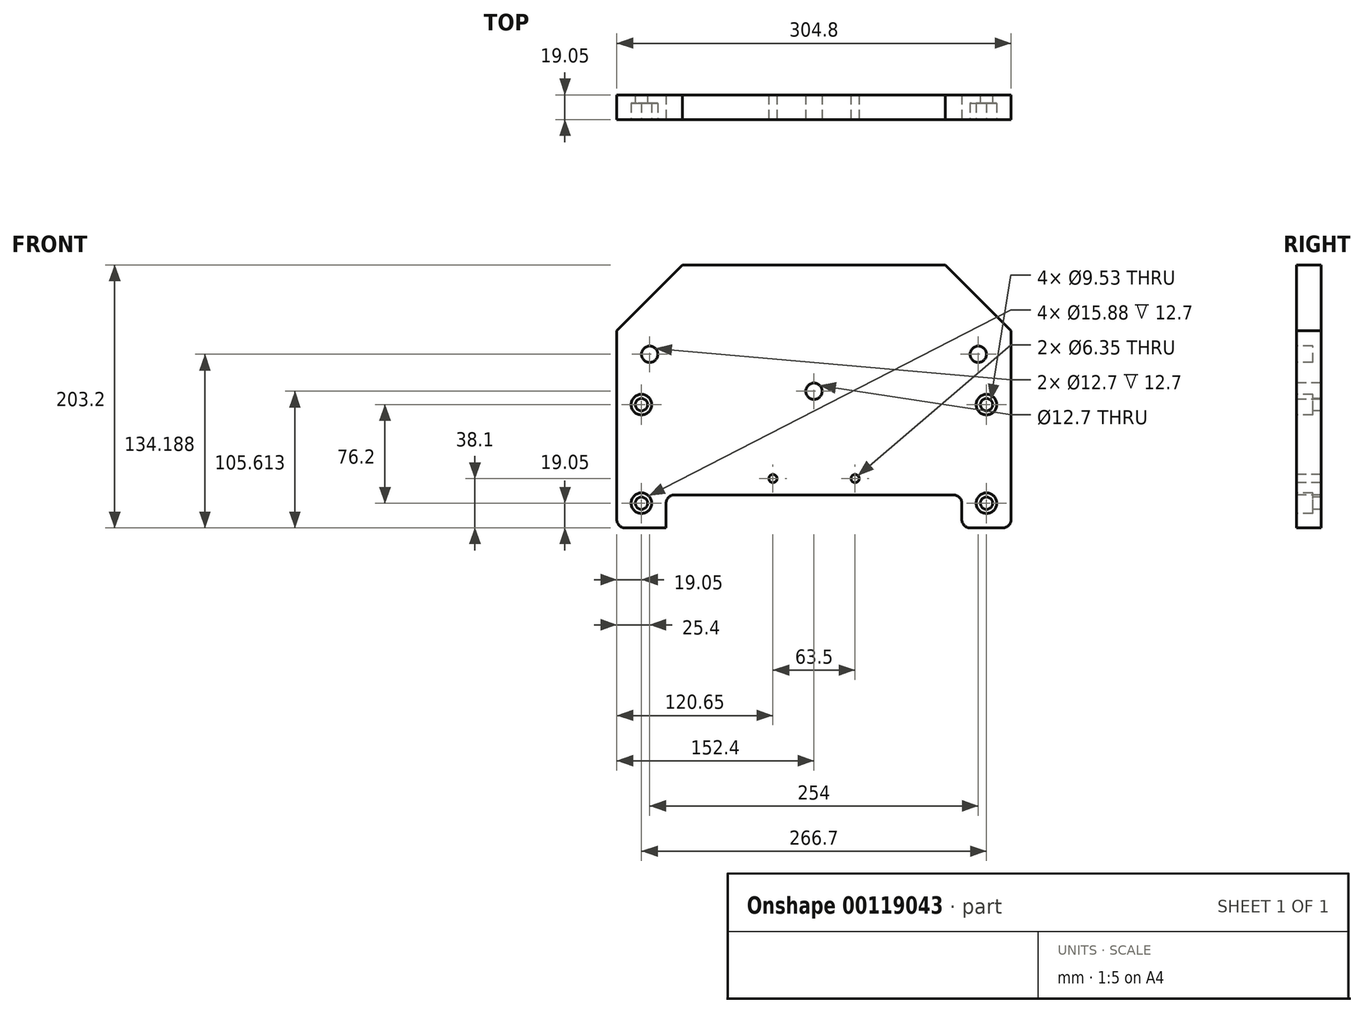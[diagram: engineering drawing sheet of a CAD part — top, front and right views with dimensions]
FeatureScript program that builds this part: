
annotation { "Feature Type Name" : "Feature", "Feature Type Description" : "" }
export const myFeature = defineFeature(function(context is Context, id is Id, definition is map)
    precondition{}
    {
        {
            var Q0;
            Q0=qCreatedBy(makeId("Front.planeOp"),FACE);
            var sketch = newSketch(context, id + "F0", { "sketchPlane" : qUnion([Q0])});
            skLineSegment(sketch, "E0.bottom", {"start": v(0, 0) * mm, "end": v(304.8, 0) * mm});
            skLineSegment(sketch, "E0.top", {"start": v(0, 203.2) * mm, "end": v(304.8, 203.2) * mm});
            skLineSegment(sketch, "E0.left", {"start": v(0, 0) * mm, "end": v(0, 203.2) * mm});
            skLineSegment(sketch, "E0.right", {"start": v(304.8, 0) * mm, "end": v(304.8, 203.2) * mm});
            skSolve(sketch);
        }
        {
            var Q0;
            Q0 = qSketchRegion(id + "F0", true);
            extrude(context, id + "F1", {"entities" : qUnion([Q0]), "depth" : 19.05 * mm});
        }
        {
            var Q0;
            Q0=makeQuery(id+"F1.opExtrude","CAP_FACE",FACE,{"disambiguationData":[OSD([sQuery(id+"F0.wireOp",EDGE,"E0.bottom"),sQuery(id+"F0.wireOp",EDGE,"E0.top"),sQuery(id+"F0.wireOp",EDGE,"E0.left"),sQuery(id+"F0.wireOp",EDGE,"E0.right")])],"isStart":false});
            var sketch = newSketch(context, id + "F2", { "sketchPlane" : qUnion([Q0])});
            skLineSegment(sketch, "E1.bottom", {"start": v(38.1, 0) * mm, "end": v(266.7, 0) * mm});
            skLineSegment(sketch, "E1.top", {"start": v(38.1, 25.4) * mm, "end": v(266.7, 25.4) * mm});
            skLineSegment(sketch, "E1.left", {"start": v(38.1, 0) * mm, "end": v(38.1, 25.4) * mm});
            skLineSegment(sketch, "E1.right", {"start": v(266.7, 0) * mm, "end": v(266.7, 25.4) * mm});
            skSolve(sketch);
        }
        {
            var Q0;
            Q0 = qSketchRegion(id + "F2", true);
            extrude(context, id + "F3", {"entities" : qUnion([Q0]), "operationType" : NewBodyOperationType.REMOVE, "endBound" : BoundingType.THROUGH_ALL, "oppositeDirection" : true, "depth" : 25.4 * mm});
        }
        {
            var Q0;
            Q0=makeQuery(id+"F1.opExtrude","CAP_FACE",FACE,{"disambiguationData":[OSD([sQuery(id+"F0.wireOp",EDGE,"E0.bottom"),sQuery(id+"F0.wireOp",EDGE,"E0.top"),sQuery(id+"F0.wireOp",EDGE,"E0.left"),sQuery(id+"F0.wireOp",EDGE,"E0.right")])],"isStart":false});
            var sketch = newSketch(context, id + "F4", { "sketchPlane" : qUnion([Q0])});
            skLineSegment(sketch, "E2", {"start": v(152.4, 203.2) * mm, "end": v(152.4, 25.4) * mm, "construction": true});
            skLineSegment(sketch, "E3", {"start": v(120.65, 38.1) * mm, "end": v(184.15, 38.1) * mm, "construction": true});
            skPoint(sketch, "E4", {"position": v(120.65, 38.1) * mm});
            skPoint(sketch, "E5", {"position": v(184.15, 38.1) * mm});
            skSolve(sketch);
        }
        {
            var Q0;
            Q0=sQuery(id+"F4.wireOp",VERTEX,"E4");
            var Q1;
            Q1=sQuery(id+"F4.wireOp",VERTEX,"E5");
            var Q2;
            Q2=makeQuery(id+"F1.opExtrude","SWEPT_BODY",BODY,{"disambiguationData":[OSD([sQuery(id+"F0.wireOp",EDGE,"E0.bottom"),sQuery(id+"F0.wireOp",EDGE,"E0.top"),sQuery(id+"F0.wireOp",EDGE,"E0.left"),sQuery(id+"F0.wireOp",EDGE,"E0.right")])]});
            hole(context, id + "F5", {"style" : HoleStyle.SIMPLE, "endStyle" : HoleEndStyle.THROUGH, "holeDiameter" : 6.35 * mm, "locations" : qUnion([Q0, Q1]), "scope" : qUnion([Q2]), "isTappedThrough" : true});
        }
        {
            var Q0;
            Q0=makeQuery(id+"F3.boolean.opBoolean","COPY",EDGE,{"derivedFrom":makeQuery(id+"F3.opExtrude","SWEPT_EDGE",EDGE,{"disambiguationData":[OSD([sQuery(id+"F2.wireOp",EDGE,"E1.top"),sQuery(id+"F2.wireOp",EDGE,"E1.left")])]})});
            var Q1;
            Q1=makeQuery(id+"F3.boolean.opBoolean","COPY",EDGE,{"derivedFrom":makeQuery(id+"F3.opExtrude","SWEPT_EDGE",EDGE,{"disambiguationData":[OSD([sQuery(id+"F2.wireOp",EDGE,"E1.top"),sQuery(id+"F2.wireOp",EDGE,"E1.right")])]})});
            var Q2;
            Q2=makeQuery(id+"F1.opExtrude","SWEPT_EDGE",EDGE,{"disambiguationData":[OSD([sQuery(id+"F0.wireOp",EDGE,"E0.bottom"),sQuery(id+"F0.wireOp",EDGE,"E0.left")])]});
            var Q3;
            Q3=makeQuery(id+"F3.boolean.opBoolean","COPY",EDGE,{"derivedFrom":makeQuery(id+"F3.opExtrude","SWEPT_EDGE",EDGE,{"disambiguationData":[OSD([sQuery(id+"F0.wireOp",EDGE,"E0.bottom"),sQuery(id+"F2.wireOp",EDGE,"E1.bottom"),sQuery(id+"F2.wireOp",EDGE,"E1.left")])]})});
            var Q4;
            Q4=makeQuery(id+"F3.boolean.opBoolean","COPY",EDGE,{"derivedFrom":makeQuery(id+"F3.opExtrude","SWEPT_EDGE",EDGE,{"disambiguationData":[OSD([sQuery(id+"F0.wireOp",EDGE,"E0.bottom"),sQuery(id+"F2.wireOp",EDGE,"E1.bottom"),sQuery(id+"F2.wireOp",EDGE,"E1.right")])]})});
            var Q5;
            Q5=makeQuery(id+"F1.opExtrude","SWEPT_EDGE",EDGE,{"disambiguationData":[OSD([sQuery(id+"F0.wireOp",EDGE,"E0.bottom"),sQuery(id+"F0.wireOp",EDGE,"E0.right")])]});
            fillet(context, id + "F6", {"entities" : qUnion([Q0, Q1, Q2, Q3, Q4, Q5]), "radius" : 6.35 * mm, "tangentPropagation" : true, "allowEdgeOverflow" : false});
        }
        {
            var Q0;
            Q0=makeQuery(id+"F1.opExtrude","CAP_FACE",FACE,{"disambiguationData":[OSD([sQuery(id+"F0.wireOp",EDGE,"E0.bottom"),sQuery(id+"F0.wireOp",EDGE,"E0.top"),sQuery(id+"F0.wireOp",EDGE,"E0.left"),sQuery(id+"F0.wireOp",EDGE,"E0.right")])],"isStart":false});
            var sketch = newSketch(context, id + "F7", { "sketchPlane" : qUnion([Q0])});
            skLineSegment(sketch, "E6", {"start": v(152.4, 25.4) * mm, "end": v(152.4, 105.61) * mm, "construction": true});
            skPoint(sketch, "E7", {"position": v(152.4, 105.61) * mm});
            skSolve(sketch);
        }
        {
            var Q0;
            Q0=sQuery(id+"F7.wireOp",VERTEX,"E7");
            var Q1;
            Q1=makeQuery(id+"F1.opExtrude","SWEPT_BODY",BODY,{"disambiguationData":[OSD([sQuery(id+"F0.wireOp",EDGE,"E0.bottom"),sQuery(id+"F0.wireOp",EDGE,"E0.top"),sQuery(id+"F0.wireOp",EDGE,"E0.left"),sQuery(id+"F0.wireOp",EDGE,"E0.right")])]});
            hole(context, id + "F8", {"style" : HoleStyle.SIMPLE, "endStyle" : HoleEndStyle.THROUGH, "holeDiameter" : 12.7 * mm, "locations" : qUnion([Q0]), "scope" : qUnion([Q1]), "isTappedThrough" : true});
        }
        {
            var Q0;
            Q0=makeQuery(id+"F1.opExtrude","CAP_FACE",FACE,{"disambiguationData":[OSD([sQuery(id+"F0.wireOp",EDGE,"E0.bottom"),sQuery(id+"F0.wireOp",EDGE,"E0.top"),sQuery(id+"F0.wireOp",EDGE,"E0.left"),sQuery(id+"F0.wireOp",EDGE,"E0.right")])],"isStart":false});
            var sketch = newSketch(context, id + "F9", { "sketchPlane" : qUnion([Q0])});
            skLineSegment(sketch, "E8", {"start": v(152.4, 105.61) * mm, "end": v(152.4, 134.19) * mm, "construction": true});
            skLineSegment(sketch, "E9", {"start": v(152.4, 134.19) * mm, "end": v(279.4, 134.19) * mm, "construction": true});
            skCircle(sketch, "E10", {"center": v(279.4, 134.19) * mm, "radius": 6.35 * mm});
            skPoint(sketch, "E11", {"position": v(215.9, 134.19) * mm});
            skCircle(sketch, "E12", {"center": v(25.4, 134.19) * mm, "radius": 6.35 * mm});
            skSolve(sketch);
        }
        {
            var Q0;
            Q0 = qSketchRegion(id + "F9", true);
            extrude(context, id + "F10", {"entities" : qUnion([Q0]), "operationType" : NewBodyOperationType.REMOVE, "oppositeDirection" : true, "depth" : 12.7 * mm});
        }
        {
            var Q0;
            Q0=makeQuery(id+"F1.opExtrude","CAP_FACE",FACE,{"disambiguationData":[OSD([sQuery(id+"F0.wireOp",EDGE,"E0.bottom"),sQuery(id+"F0.wireOp",EDGE,"E0.top"),sQuery(id+"F0.wireOp",EDGE,"E0.left"),sQuery(id+"F0.wireOp",EDGE,"E0.right")])],"isStart":false});
            var sketch = newSketch(context, id + "F11", { "sketchPlane" : qUnion([Q0])});
            skPoint(sketch, "E13", {"position": v(19.05, 19.05) * mm});
            skPoint(sketch, "E14", {"position": v(19.05, 95.25) * mm});
            skPoint(sketch, "E15", {"position": v(285.75, 19.05) * mm});
            skPoint(sketch, "E16", {"position": v(285.75, 95.25) * mm});
            skSolve(sketch);
        }
        {
            var Q0;
            Q0=sQuery(id+"F11.wireOp",VERTEX,"E14");
            var Q1;
            Q1=sQuery(id+"F11.wireOp",VERTEX,"E13");
            var Q2;
            Q2=sQuery(id+"F11.wireOp",VERTEX,"E15");
            var Q3;
            Q3=sQuery(id+"F11.wireOp",VERTEX,"E16");
            var Q4;
            Q4=makeQuery(id+"F1.opExtrude","SWEPT_BODY",BODY,{"disambiguationData":[OSD([sQuery(id+"F0.wireOp",EDGE,"E0.bottom"),sQuery(id+"F0.wireOp",EDGE,"E0.top"),sQuery(id+"F0.wireOp",EDGE,"E0.left"),sQuery(id+"F0.wireOp",EDGE,"E0.right")])]});
            hole(context, id + "F12", {"style" : HoleStyle.C_BORE, "endStyle" : HoleEndStyle.THROUGH, "holeDiameter" : 9.52 * mm, "cBoreDiameter" : 15.88 * mm, "cBoreDepth" : 12.7 * mm, "locations" : qUnion([Q0, Q1, Q2, Q3]), "scope" : qUnion([Q4]), "isTappedThrough" : true});
        }
        {
            var Q0;
            Q0=makeQuery(id+"F1.opExtrude","SWEPT_EDGE",EDGE,{"disambiguationData":[OSD([sQuery(id+"F0.wireOp",EDGE,"E0.top"),sQuery(id+"F0.wireOp",EDGE,"E0.left")])]});
            var Q1;
            Q1=makeQuery(id+"F1.opExtrude","SWEPT_EDGE",EDGE,{"disambiguationData":[OSD([sQuery(id+"F0.wireOp",EDGE,"E0.top"),sQuery(id+"F0.wireOp",EDGE,"E0.right")])]});
            chamfer(context, id + "F13", {"entities" : qUnion([Q0, Q1]), "width" : 50.8 * mm, "tangentPropagation" : true});
        }
    });
